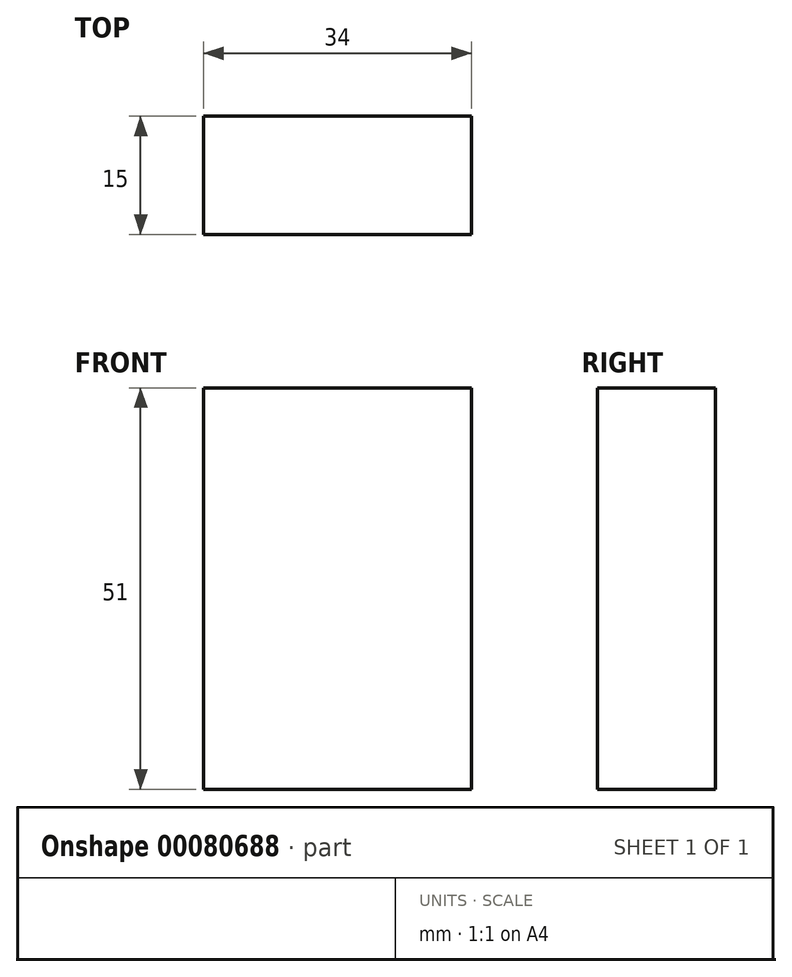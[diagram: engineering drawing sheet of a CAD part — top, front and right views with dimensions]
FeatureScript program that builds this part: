
annotation { "Feature Type Name" : "Feature", "Feature Type Description" : "" }
export const myFeature = defineFeature(function(context is Context, id is Id, definition is map)
    precondition{}
    {
        {
            var Q0;
            Q0=qCreatedBy(makeId("Front.planeOp"),FACE);
            var sketch = newSketch(context, id + "F0", { "sketchPlane" : qUnion([Q0])});
            skLineSegment(sketch, "E0.bottom", {"start": v(-17, 25.5) * mm, "end": v(17, 25.5) * mm});
            skLineSegment(sketch, "E0.top", {"start": v(-17, -25.5) * mm, "end": v(17, -25.5) * mm});
            skLineSegment(sketch, "E0.left", {"start": v(-17, 25.5) * mm, "end": v(-17, -25.5) * mm});
            skLineSegment(sketch, "E0.right", {"start": v(17, 25.5) * mm, "end": v(17, -25.5) * mm});
            skPoint(sketch, "E0.middle", {"position": v(0, 0) * mm});
            skSolve(sketch);
        }
        {
            var Q0;
            Q0=makeQuery(id+"F0.imprint","IMPRINT",FACE,{"disambiguationData":[TD([[makeQuery(id+"F0.imprint","IMPRINT",EDGE,{"derivedFrom":sQuery(id+"F0.wireOp",EDGE,"E0.bottom")}),-1.0]])]});
            extrude(context, id + "F1", {"entities" : qUnion([Q0]), "depth" : 15 * mm});
        }
    });
